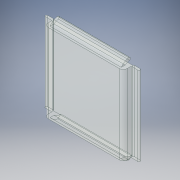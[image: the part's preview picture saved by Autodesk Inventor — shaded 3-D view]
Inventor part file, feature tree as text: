
AUTODESK INVENTOR PART (.ipt)
format: ipt  version: 2019 (Build 230136000, 136)  size: 159,232 bytes
history: native  units: mm
features: sketch x4, fillet x3, extrude x2, sweep x1, mirror x1, plane x1, projected_geometry x1
ambient origin geometry x8: Origin, YZ Plane, XZ Plane, XY Plane, X Axis, Y Axis, Z Axis, Center Point
bodies: Solid1 (feature_tree)
feature tree (13):
  extrude  "Extrusion1"  Depth=100.0mm
  sweep  "Sweep1"
  mirror  "Mirror1"
  fillet  "Fillet2"  Radius=5.0mm
  plane  "Work Plane1"
  extrude  "Extrusion3"  Depth=5.0mm
  fillet  "Fillet3"  [1 undecoded]
  fillet  "Fillet4"  Radius=10.0mm
  sketch  "Sketch1"  dims[d0=100.0mm d1=100.0mm]
  sketch  "Sketch2"  dims[d2=12.0mm d3=0.0mm d4=90.0mm d5=5.0mm]
  projected_geometry  "Projected Loop1"
  sketch  "Sketch3"  dims[d8=0.0mm d9=0.0mm d11=5.0mm d16=-10.0mm d17=10.0mm]
  sketch  "Sketch5"  dims[d18=100.0mm d19=3.0mm d20=0.0mm d21=1.5mm d24=1.5mm]
note: 1 required parameter value undecoded (feature->parameter linkage not recoverable at this tier; creation-order binding heuristic only, values carry confidence <= 0.55)
